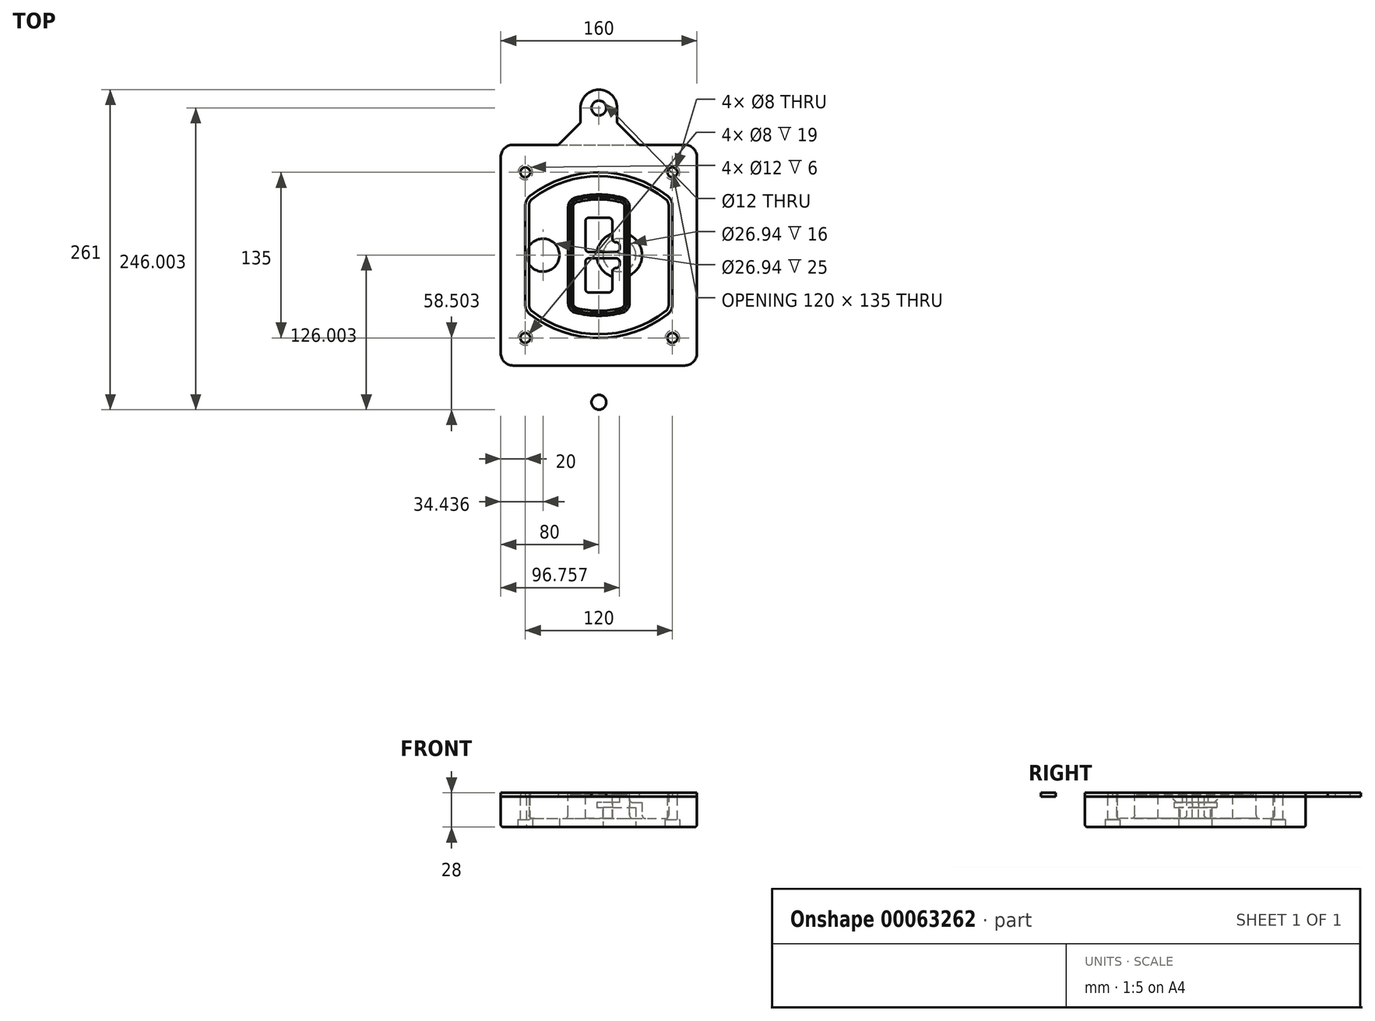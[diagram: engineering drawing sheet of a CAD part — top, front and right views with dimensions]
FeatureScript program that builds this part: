
annotation { "Feature Type Name" : "Feature", "Feature Type Description" : "" }
export const myFeature = defineFeature(function(context is Context, id is Id, definition is map)
    precondition{}
    {
        {
            var Q0;
            Q0=qCreatedBy(makeId("Top.planeOp"),FACE);
            var sketch = newSketch(context, id + "F0", { "sketchPlane" : qUnion([Q0])});
            skPoint(sketch, "E0.rect.middle", {"position": v(0, 0) * mm});
            skLineSegment(sketch, "E1.bottom", {"start": v(24.05, 28.38) * mm, "end": v(164.05, 28.38) * mm});
            skLineSegment(sketch, "E1.top", {"start": v(24.05, 208.38) * mm, "end": v(164.05, 208.38) * mm});
            skLineSegment(sketch, "E1.left", {"start": v(14.05, 38.38) * mm, "end": v(14.05, 198.38) * mm});
            skLineSegment(sketch, "E1.right", {"start": v(174.05, 38.38) * mm, "end": v(174.05, 198.38) * mm});
            skLineSegment(sketch, "E2", {"start": v(14.05, 208.38) * mm, "end": v(174.05, 28.38) * mm, "construction": true});
            skLineSegment(sketch, "E3", {"start": v(174.05, 208.38) * mm, "end": v(14.05, 28.38) * mm, "construction": true});
            skCircle(sketch, "E4", {"center": v(34.05, 185.88) * mm, "radius": 4 * mm});
            skCircle(sketch, "E5", {"center": v(154.05, 185.88) * mm, "radius": 4 * mm});
            skCircle(sketch, "E6", {"center": v(154.05, 50.88) * mm, "radius": 4 * mm});
            skCircle(sketch, "E7", {"center": v(34.05, 50.88) * mm, "radius": 4 * mm});
            skLineSegment(sketch, "E8", {"start": v(34.05, 185.88) * mm, "end": v(154.05, 185.88) * mm, "construction": true});
            skLineSegment(sketch, "E9", {"start": v(154.05, 185.88) * mm, "end": v(154.05, 50.88) * mm, "construction": true});
            skLineSegment(sketch, "E10", {"start": v(154.05, 50.88) * mm, "end": v(34.05, 50.88) * mm, "construction": true});
            skLineSegment(sketch, "E11", {"start": v(34.05, 50.88) * mm, "end": v(34.05, 185.88) * mm, "construction": true});
            skLineSegment(sketch, "E12", {"start": v(34.05, 158.68) * mm, "end": v(34.05, 78.09) * mm});
            skLineSegment(sketch, "E13", {"start": v(154.05, 158.68) * mm, "end": v(154.05, 78.09) * mm});
            skArc(sketch, "E14", {"start": v(150.2, 166.56) * mm, "mid": v(94.05, 185.88) * mm, "end": v(37.9, 166.56) * mm});
            skArc(sketch, "E15", {"start": v(37.9, 70.2) * mm, "mid": v(94.05, 50.88) * mm, "end": v(150.2, 70.2) * mm});
            skLineSegment(sketch, "E16", {"start": v(34.05, 118.38) * mm, "end": v(154.05, 118.38) * mm, "construction": true});
            skPoint(sketch, "E17.visualSharp", {"position": v(34.05, 73.38) * mm});
            skArc(sketch, "E17.filletArc", {"start": v(34.05, 78.09) * mm, "mid": v(35.06, 73.7) * mm, "end": v(37.9, 70.2) * mm});
            skPoint(sketch, "E18.visualSharp", {"position": v(34.05, 163.38) * mm});
            skArc(sketch, "E18.filletArc", {"start": v(37.9, 166.56) * mm, "mid": v(35.06, 163.06) * mm, "end": v(34.05, 158.68) * mm});
            skPoint(sketch, "E19.visualSharp", {"position": v(154.05, 163.38) * mm});
            skArc(sketch, "E19.filletArc", {"start": v(154.05, 158.68) * mm, "mid": v(153.04, 163.06) * mm, "end": v(150.2, 166.56) * mm});
            skPoint(sketch, "E20.visualSharp", {"position": v(154.05, 73.38) * mm});
            skArc(sketch, "E20.filletArc", {"start": v(150.2, 70.2) * mm, "mid": v(153.04, 73.7) * mm, "end": v(154.05, 78.09) * mm});
            skPoint(sketch, "E21.visualSharp", {"position": v(14.05, 208.38) * mm});
            skArc(sketch, "E21.filletArc", {"start": v(24.05, 208.38) * mm, "mid": v(16.98, 205.45) * mm, "end": v(14.05, 198.38) * mm});
            skPoint(sketch, "E22.visualSharp", {"position": v(174.05, 208.38) * mm});
            skArc(sketch, "E22.filletArc", {"start": v(174.05, 198.38) * mm, "mid": v(171.12, 205.45) * mm, "end": v(164.05, 208.38) * mm});
            skPoint(sketch, "E23.visualSharp", {"position": v(174.05, 28.38) * mm});
            skArc(sketch, "E23.filletArc", {"start": v(164.05, 28.38) * mm, "mid": v(171.12, 31.31) * mm, "end": v(174.05, 38.38) * mm});
            skPoint(sketch, "E24.visualSharp", {"position": v(14.05, 28.38) * mm});
            skArc(sketch, "E24.filletArc", {"start": v(14.05, 38.38) * mm, "mid": v(16.98, 31.31) * mm, "end": v(24.05, 28.38) * mm});
            skArc(sketch, "E25.0", {"start": v(151.05, 158.68) * mm, "mid": v(150.34, 161.75) * mm, "end": v(148.36, 164.2) * mm});
            skLineSegment(sketch, "E25.1", {"start": v(151.05, 158.68) * mm, "end": v(151.05, 78.09) * mm});
            skArc(sketch, "E25.2", {"start": v(148.36, 72.57) * mm, "mid": v(150.34, 75.02) * mm, "end": v(151.05, 78.09) * mm});
            skArc(sketch, "E25.3", {"start": v(39.74, 72.57) * mm, "mid": v(94.05, 53.88) * mm, "end": v(148.36, 72.57) * mm});
            skArc(sketch, "E25.4", {"start": v(37.05, 78.09) * mm, "mid": v(37.76, 75.02) * mm, "end": v(39.74, 72.57) * mm});
            skArc(sketch, "E25.5", {"start": v(148.36, 164.2) * mm, "mid": v(94.05, 182.88) * mm, "end": v(39.74, 164.2) * mm});
            skLineSegment(sketch, "E25.6", {"start": v(37.05, 158.68) * mm, "end": v(37.05, 78.09) * mm});
            skArc(sketch, "E25.7", {"start": v(39.74, 164.2) * mm, "mid": v(37.76, 161.75) * mm, "end": v(37.05, 158.68) * mm});
            skArc(sketch, "E26.0", {"start": v(35.43, 169.71) * mm, "mid": v(31.47, 164.82) * mm, "end": v(30.05, 158.68) * mm});
            skArc(sketch, "E26.1", {"start": v(152.67, 169.71) * mm, "mid": v(94.05, 189.88) * mm, "end": v(35.43, 169.71) * mm});
            skArc(sketch, "E26.2", {"start": v(158.05, 158.68) * mm, "mid": v(156.63, 164.82) * mm, "end": v(152.67, 169.71) * mm});
            skLineSegment(sketch, "E26.3", {"start": v(158.05, 158.68) * mm, "end": v(158.05, 78.09) * mm});
            skArc(sketch, "E26.4", {"start": v(152.67, 67.05) * mm, "mid": v(156.63, 71.95) * mm, "end": v(158.05, 78.09) * mm});
            skLineSegment(sketch, "E26.5", {"start": v(30.05, 158.68) * mm, "end": v(30.05, 78.09) * mm});
            skArc(sketch, "E26.6", {"start": v(35.43, 67.05) * mm, "mid": v(94.05, 46.88) * mm, "end": v(152.67, 67.05) * mm});
            skArc(sketch, "E26.7", {"start": v(30.05, 78.09) * mm, "mid": v(31.47, 71.95) * mm, "end": v(35.43, 67.05) * mm});
            skSolve(sketch);
        }
        {
            var Q0;
            Q0=makeQuery(id+"F0.imprint","IMPRINT",FACE,{"disambiguationData":[TD([[makeQuery(id+"F0.imprint","IMPRINT",EDGE,{"derivedFrom":sQuery(id+"F0.wireOp",EDGE,"E1.bottom")}),1.0]])]});
            var Q1;
            Q1=makeQuery(id+"F0.imprint","IMPRINT",FACE,{"disambiguationData":[TD([[makeQuery(id+"F0.imprint","IMPRINT",EDGE,{"derivedFrom":sQuery(id+"F0.wireOp",EDGE,"E12")}),1.0]])]});
            var Q2;
            Q2=makeQuery(id+"F0.imprint","IMPRINT",FACE,{"disambiguationData":[TD([[makeQuery(id+"F0.imprint","IMPRINT",EDGE,{"derivedFrom":sQuery(id+"F0.wireOp",EDGE,"E25.0")}),1.0]])]});
            var Q3;
            Q3=makeQuery(id+"F0.imprint","IMPRINT",FACE,{"disambiguationData":[TD([[makeQuery(id+"F0.imprint","IMPRINT",EDGE,{"derivedFrom":sQuery(id+"F0.wireOp",EDGE,"E12")}),-1.0]])]});
            extrude(context, id + "F1", {"entities" : qUnion([Q0, Q1, Q2, Q3]), "oppositeDirection" : true, "depth" : 25 * mm});
        }
        {
            var Q0;
            Q0=makeQuery(id+"F0.imprint","IMPRINT",FACE,{"disambiguationData":[TD([[makeQuery(id+"F0.imprint","IMPRINT",EDGE,{"derivedFrom":sQuery(id+"F0.wireOp",EDGE,"E12")}),1.0]])]});
            extrude(context, id + "F2", {"entities" : qUnion([Q0]), "operationType" : NewBodyOperationType.ADD, "depth" : 3 * mm});
        }
        {
            var Q0;
            Q0=makeQuery(id+"F0.imprint","IMPRINT",FACE,{"disambiguationData":[TD([[makeQuery(id+"F0.imprint","IMPRINT",EDGE,{"derivedFrom":sQuery(id+"F0.wireOp",EDGE,"E25.0")}),1.0]])]});
            extrude(context, id + "F3", {"entities" : qUnion([Q0]), "operationType" : NewBodyOperationType.REMOVE, "oppositeDirection" : true, "depth" : 18 * mm});
        }
        {
            var Q0;
            Q0=makeQuery(id+"F2.opExtrude","CAP_FACE",FACE,{"disambiguationData":[OSD([sQuery(id+"F0.wireOp",EDGE,"E12"),sQuery(id+"F0.wireOp",EDGE,"E13"),sQuery(id+"F0.wireOp",EDGE,"E14"),sQuery(id+"F0.wireOp",EDGE,"E15"),sQuery(id+"F0.wireOp",EDGE,"E17.filletArc"),sQuery(id+"F0.wireOp",EDGE,"E18.filletArc"),sQuery(id+"F0.wireOp",EDGE,"E19.filletArc"),sQuery(id+"F0.wireOp",EDGE,"E20.filletArc"),sQuery(id+"F0.wireOp",EDGE,"E25.0"),sQuery(id+"F0.wireOp",EDGE,"E25.1"),sQuery(id+"F0.wireOp",EDGE,"E25.2"),sQuery(id+"F0.wireOp",EDGE,"E25.3"),sQuery(id+"F0.wireOp",EDGE,"E25.4"),sQuery(id+"F0.wireOp",EDGE,"E25.5"),sQuery(id+"F0.wireOp",EDGE,"E25.6"),sQuery(id+"F0.wireOp",EDGE,"E25.7")])],"isStart":false});
            var sketch = newSketch(context, id + "F4", { "sketchPlane" : qUnion([Q0])});
            skArc(sketch, "E27.0", {"start": v(74.97, 71.41) * mm, "mid": v(94.05, 68.88) * mm, "end": v(113.13, 71.41) * mm});
            skArc(sketch, "E28.0", {"start": v(113.13, 165.35) * mm, "mid": v(94.05, 167.88) * mm, "end": v(74.97, 165.35) * mm});
            skLineSegment(sketch, "E29", {"start": v(69.05, 157.63) * mm, "end": v(69.05, 79.14) * mm});
            skLineSegment(sketch, "E30", {"start": v(119.05, 157.63) * mm, "end": v(119.05, 79.14) * mm});
            skLineSegment(sketch, "E31", {"start": v(69.05, 163.48) * mm, "end": v(119.05, 163.48) * mm, "construction": true});
            skLineSegment(sketch, "E32", {"start": v(69.05, 73.28) * mm, "end": v(119.05, 73.28) * mm, "construction": true});
            skPoint(sketch, "E33.visualSharp", {"position": v(69.05, 163.48) * mm});
            skArc(sketch, "E33.filletArc", {"start": v(74.97, 165.35) * mm, "mid": v(70.7, 162.5) * mm, "end": v(69.05, 157.63) * mm});
            skPoint(sketch, "E34.visualSharp", {"position": v(119.05, 163.48) * mm});
            skArc(sketch, "E34.filletArc", {"start": v(119.05, 157.63) * mm, "mid": v(117.4, 162.5) * mm, "end": v(113.13, 165.35) * mm});
            skPoint(sketch, "E35.visualSharp", {"position": v(119.05, 73.28) * mm});
            skArc(sketch, "E35.filletArc", {"start": v(113.13, 71.41) * mm, "mid": v(117.4, 74.27) * mm, "end": v(119.05, 79.14) * mm});
            skPoint(sketch, "E36.visualSharp", {"position": v(69.05, 73.28) * mm});
            skArc(sketch, "E36.filletArc", {"start": v(69.05, 79.14) * mm, "mid": v(70.7, 74.27) * mm, "end": v(74.97, 71.41) * mm});
            skArc(sketch, "E37.0", {"start": v(148.36, 164.2) * mm, "mid": v(94.05, 182.88) * mm, "end": v(39.74, 164.2) * mm});
            skArc(sketch, "E37.1", {"start": v(39.74, 164.2) * mm, "mid": v(37.76, 161.75) * mm, "end": v(37.05, 158.68) * mm});
            skLineSegment(sketch, "E37.2", {"start": v(37.05, 158.68) * mm, "end": v(37.05, 78.09) * mm});
            skArc(sketch, "E37.3", {"start": v(37.05, 78.09) * mm, "mid": v(37.76, 75.02) * mm, "end": v(39.74, 72.57) * mm});
            skArc(sketch, "E37.4", {"start": v(39.74, 72.57) * mm, "mid": v(94.05, 53.88) * mm, "end": v(148.36, 72.57) * mm});
            skArc(sketch, "E37.5", {"start": v(148.36, 72.57) * mm, "mid": v(150.34, 75.02) * mm, "end": v(151.05, 78.09) * mm});
            skLineSegment(sketch, "E37.6", {"start": v(151.05, 158.68) * mm, "end": v(151.05, 78.09) * mm});
            skArc(sketch, "E37.7", {"start": v(151.05, 158.68) * mm, "mid": v(150.34, 161.75) * mm, "end": v(148.36, 164.2) * mm});
            skLineSegment(sketch, "E38.0", {"start": v(117.05, 157.63) * mm, "end": v(117.05, 79.14) * mm});
            skArc(sketch, "E38.1", {"start": v(112.61, 73.34) * mm, "mid": v(115.81, 75.49) * mm, "end": v(117.05, 79.14) * mm});
            skArc(sketch, "E38.2", {"start": v(75.49, 73.34) * mm, "mid": v(94.05, 70.88) * mm, "end": v(112.61, 73.34) * mm});
            skArc(sketch, "E38.3", {"start": v(71.05, 79.14) * mm, "mid": v(72.29, 75.49) * mm, "end": v(75.49, 73.34) * mm});
            skLineSegment(sketch, "E38.4", {"start": v(71.05, 157.63) * mm, "end": v(71.05, 79.14) * mm});
            skArc(sketch, "E38.5", {"start": v(117.05, 157.63) * mm, "mid": v(115.81, 161.28) * mm, "end": v(112.61, 163.42) * mm});
            skArc(sketch, "E38.6", {"start": v(75.49, 163.42) * mm, "mid": v(72.29, 161.28) * mm, "end": v(71.05, 157.63) * mm});
            skArc(sketch, "E38.7", {"start": v(112.61, 163.42) * mm, "mid": v(94.05, 165.88) * mm, "end": v(75.49, 163.42) * mm});
            skArc(sketch, "E39.0", {"start": v(115.05, 157.63) * mm, "mid": v(114.23, 160.06) * mm, "end": v(112.1, 161.5) * mm});
            skLineSegment(sketch, "E39.1", {"start": v(115.05, 157.63) * mm, "end": v(115.05, 79.14) * mm});
            skArc(sketch, "E39.2", {"start": v(112.1, 75.27) * mm, "mid": v(114.23, 76.7) * mm, "end": v(115.05, 79.14) * mm});
            skArc(sketch, "E39.3", {"start": v(76, 75.27) * mm, "mid": v(94.05, 72.88) * mm, "end": v(112.1, 75.27) * mm});
            skArc(sketch, "E39.4", {"start": v(73.05, 79.14) * mm, "mid": v(73.87, 76.7) * mm, "end": v(76, 75.27) * mm});
            skArc(sketch, "E39.5", {"start": v(112.1, 161.5) * mm, "mid": v(94.05, 163.88) * mm, "end": v(76, 161.5) * mm});
            skLineSegment(sketch, "E39.6", {"start": v(73.05, 157.63) * mm, "end": v(73.05, 79.14) * mm});
            skArc(sketch, "E39.7", {"start": v(76, 161.5) * mm, "mid": v(73.87, 160.06) * mm, "end": v(73.05, 157.63) * mm});
            skLineSegment(sketch, "E40", {"start": v(69.05, 118.38) * mm, "end": v(119.05, 118.38) * mm, "construction": true});
            skLineSegment(sketch, "E41", {"start": v(83.05, 123.88) * mm, "end": v(83.05, 145.88) * mm});
            skLineSegment(sketch, "E42", {"start": v(86.05, 148.88) * mm, "end": v(102.05, 148.88) * mm});
            skLineSegment(sketch, "E43", {"start": v(105.05, 145.88) * mm, "end": v(105.05, 131.88) * mm});
            skLineSegment(sketch, "E44", {"start": v(108.05, 128.88) * mm, "end": v(108.05, 128.88) * mm});
            skLineSegment(sketch, "E45", {"start": v(111.05, 125.88) * mm, "end": v(111.05, 123.88) * mm});
            skLineSegment(sketch, "E46", {"start": v(108.05, 120.88) * mm, "end": v(86.05, 120.88) * mm});
            skPoint(sketch, "E47.visualSharp", {"position": v(83.05, 148.88) * mm});
            skArc(sketch, "E47.filletArc", {"start": v(86.05, 148.88) * mm, "mid": v(83.93, 148) * mm, "end": v(83.05, 145.88) * mm});
            skPoint(sketch, "E48.visualSharp", {"position": v(105.05, 148.88) * mm});
            skArc(sketch, "E48.filletArc", {"start": v(105.05, 145.88) * mm, "mid": v(104.17, 148) * mm, "end": v(102.05, 148.88) * mm});
            skPoint(sketch, "E49.visualSharp", {"position": v(105.05, 128.88) * mm});
            skArc(sketch, "E49.filletArc", {"start": v(105.05, 131.88) * mm, "mid": v(105.93, 129.76) * mm, "end": v(108.05, 128.88) * mm});
            skPoint(sketch, "E50.visualSharp", {"position": v(111.05, 128.88) * mm});
            skArc(sketch, "E50.filletArc", {"start": v(111.05, 125.88) * mm, "mid": v(110.17, 128) * mm, "end": v(108.05, 128.88) * mm});
            skPoint(sketch, "E51.visualSharp", {"position": v(111.05, 120.88) * mm});
            skArc(sketch, "E51.filletArc", {"start": v(108.05, 120.88) * mm, "mid": v(110.17, 121.76) * mm, "end": v(111.05, 123.88) * mm});
            skPoint(sketch, "E52.visualSharp", {"position": v(83.05, 120.88) * mm});
            skArc(sketch, "E52.filletArc", {"start": v(83.05, 123.88) * mm, "mid": v(83.93, 121.76) * mm, "end": v(86.05, 120.88) * mm});
            skLineSegment(sketch, "E53.0.MirrorCS", {"start": v(108.05, 115.88) * mm, "end": v(86.05, 115.88) * mm});
            skArc(sketch, "E54.0.MirrorCS", {"start": v(83.05, 112.88) * mm, "mid": v(83.93, 115) * mm, "end": v(86.05, 115.88) * mm});
            skLineSegment(sketch, "E55.0.MirrorCS", {"start": v(83.05, 112.88) * mm, "end": v(83.05, 90.88) * mm});
            skArc(sketch, "E56.0.MirrorCS", {"start": v(86.05, 87.88) * mm, "mid": v(83.93, 88.76) * mm, "end": v(83.05, 90.88) * mm});
            skLineSegment(sketch, "E57.0.MirrorCS", {"start": v(86.05, 87.88) * mm, "end": v(102.05, 87.88) * mm});
            skArc(sketch, "E58.0.MirrorCS", {"start": v(105.05, 90.88) * mm, "mid": v(104.17, 88.76) * mm, "end": v(102.05, 87.88) * mm});
            skLineSegment(sketch, "E59.0.MirrorCS", {"start": v(105.05, 90.88) * mm, "end": v(105.05, 104.88) * mm});
            skArc(sketch, "E60.0.MirrorCS", {"start": v(105.05, 104.88) * mm, "mid": v(105.93, 107) * mm, "end": v(108.05, 107.88) * mm});
            skArc(sketch, "E61.0.MirrorCS", {"start": v(111.05, 110.88) * mm, "mid": v(110.17, 108.76) * mm, "end": v(108.05, 107.88) * mm});
            skLineSegment(sketch, "E62.0.MirrorCS", {"start": v(111.05, 110.88) * mm, "end": v(111.05, 112.88) * mm});
            skArc(sketch, "E63.0.MirrorCS", {"start": v(108.05, 115.88) * mm, "mid": v(110.17, 115) * mm, "end": v(111.05, 112.88) * mm});
            skSolve(sketch);
        }
        {
            var Q0;
            Q0=makeQuery(id+"F4.imprint","IMPRINT",FACE,{"disambiguationData":[TD([[makeQuery(id+"F4.imprint","IMPRINT",EDGE,{"derivedFrom":sQuery(id+"F4.wireOp",EDGE,"E27.0")}),1.0]])]});
            var Q1;
            Q1=makeQuery(id+"F4.imprint","IMPRINT",FACE,{"disambiguationData":[TD([[makeQuery(id+"F4.imprint","IMPRINT",EDGE,{"derivedFrom":sQuery(id+"F4.wireOp",EDGE,"E38.0")}),-1.0]])]});
            var Q2;
            Q2=makeQuery(id+"F4.imprint","IMPRINT",FACE,{"disambiguationData":[TD([[makeQuery(id+"F4.imprint","IMPRINT",EDGE,{"derivedFrom":sQuery(id+"F4.wireOp",EDGE,"E39.0")}),1.0]])]});
            extrude(context, id + "F5", {"entities" : qUnion([Q0, Q1, Q2]), "operationType" : NewBodyOperationType.ADD, "endBound" : BoundingType.UP_TO_NEXT, "oppositeDirection" : true, "depth" : 25 * mm});
        }
        {
            var Q0;
            Q0=makeQuery(id+"F4.imprint","IMPRINT",FACE,{"disambiguationData":[TD([[makeQuery(id+"F4.imprint","IMPRINT",EDGE,{"derivedFrom":sQuery(id+"F4.wireOp",EDGE,"E38.0")}),-1.0]])]});
            extrude(context, id + "F6", {"entities" : qUnion([Q0]), "operationType" : NewBodyOperationType.REMOVE, "oppositeDirection" : true, "depth" : 2 * mm});
        }
        {
            var Q0;
            Q0=makeQuery(id+"F1.opExtrude","CAP_FACE",FACE,{"disambiguationData":[OSD([sQuery(id+"F0.wireOp",EDGE,"E1.bottom"),sQuery(id+"F0.wireOp",EDGE,"E1.top"),sQuery(id+"F0.wireOp",EDGE,"E1.left"),sQuery(id+"F0.wireOp",EDGE,"E1.right"),sQuery(id+"F0.wireOp",EDGE,"E4"),sQuery(id+"F0.wireOp",EDGE,"E5"),sQuery(id+"F0.wireOp",EDGE,"E6"),sQuery(id+"F0.wireOp",EDGE,"E7"),sQuery(id+"F0.wireOp",EDGE,"E21.filletArc"),sQuery(id+"F0.wireOp",EDGE,"E22.filletArc"),sQuery(id+"F0.wireOp",EDGE,"E23.filletArc"),sQuery(id+"F0.wireOp",EDGE,"E24.filletArc")])],"isStart":false});
            var sketch = newSketch(context, id + "F7", { "sketchPlane" : qUnion([Q0])});
            skCircle(sketch, "E64", {"center": v(110.8, -118.38) * mm, "radius": 13.47 * mm});
            skCircle(sketch, "E65", {"center": v(48.49, -118.38) * mm, "radius": 13.47 * mm});
            skLineSegment(sketch, "E66", {"start": v(174.05, -118.38) * mm, "end": v(14.05, -118.38) * mm});
            skCircle(sketch, "E67", {"center": v(110.8, -118.38) * mm, "radius": 18.47 * mm});
            skCircle(sketch, "E68", {"center": v(154.05, -185.88) * mm, "radius": 6 * mm});
            skCircle(sketch, "E69", {"center": v(34.05, -185.88) * mm, "radius": 6 * mm});
            skCircle(sketch, "E70", {"center": v(34.05, -50.88) * mm, "radius": 6 * mm});
            skCircle(sketch, "E71", {"center": v(154.05, -50.88) * mm, "radius": 6 * mm});
            skSolve(sketch);
        }
        {
            var Q0;
            {var subQ1=sQuery(id+"F7.wireOp",EDGE,"E66");var subQ4=sQuery(id+"F7.wireOp",EDGE,"E64");var subQ6=makeQuery(id+"F7.imprint","INTERSECT",VERTEX,{"disambiguationData":[OD(0.0)],"derivedFrom":[subQ4,subQ1]});Q0=makeQuery(id+"F7.imprint","IMPRINT",FACE,{"disambiguationData":[TD([[makeQuery(id+"F7.imprint","IMPRINT",EDGE,{"disambiguationData":[TD([[subQ6,-1.0]])],"derivedFrom":subQ4}),-1.0]])]});}
            var Q1;
            {var subQ0=sQuery(id+"F7.wireOp",EDGE,"E66");var subQ1=sQuery(id+"F7.wireOp",EDGE,"E64");var subQ3=makeQuery(id+"F7.imprint","INTERSECT",VERTEX,{"disambiguationData":[OD(0.0)],"derivedFrom":[subQ1,subQ0]});Q1=makeQuery(id+"F7.imprint","IMPRINT",FACE,{"disambiguationData":[TD([[makeQuery(id+"F7.imprint","IMPRINT",EDGE,{"disambiguationData":[TD([[subQ3,-1.0]])],"derivedFrom":subQ1}),1.0]])]});}
            var Q2;
            {var subQ0=sQuery(id+"F7.wireOp",EDGE,"E66");var subQ1=sQuery(id+"F7.wireOp",EDGE,"E64");var subQ3=makeQuery(id+"F7.imprint","INTERSECT",VERTEX,{"disambiguationData":[OD(0.0)],"derivedFrom":[subQ1,subQ0]});Q2=makeQuery(id+"F7.imprint","IMPRINT",FACE,{"disambiguationData":[TD([[makeQuery(id+"F7.imprint","IMPRINT",EDGE,{"disambiguationData":[TD([[subQ3,1.0]])],"derivedFrom":subQ1}),1.0]])]});}
            var Q3;
            {var subQ1=sQuery(id+"F7.wireOp",EDGE,"E66");var subQ4=sQuery(id+"F7.wireOp",EDGE,"E64");var subQ6=makeQuery(id+"F7.imprint","INTERSECT",VERTEX,{"disambiguationData":[OD(0.0)],"derivedFrom":[subQ4,subQ1]});Q3=makeQuery(id+"F7.imprint","IMPRINT",FACE,{"disambiguationData":[TD([[makeQuery(id+"F7.imprint","IMPRINT",EDGE,{"disambiguationData":[TD([[subQ6,1.0]])],"derivedFrom":subQ4}),-1.0]])]});}
            extrude(context, id + "F8", {"entities" : qUnion([Q0, Q1, Q2, Q3]), "operationType" : NewBodyOperationType.ADD, "oppositeDirection" : true, "depth" : 20 * mm});
        }
        {
            var Q0;
            {var subQ0=sQuery(id+"F7.wireOp",EDGE,"E66");var subQ1=sQuery(id+"F7.wireOp",EDGE,"E64");var subQ3=makeQuery(id+"F7.imprint","INTERSECT",VERTEX,{"disambiguationData":[OD(0.0)],"derivedFrom":[subQ1,subQ0]});Q0=makeQuery(id+"F7.imprint","IMPRINT",FACE,{"disambiguationData":[TD([[makeQuery(id+"F7.imprint","IMPRINT",EDGE,{"disambiguationData":[TD([[subQ3,-1.0]])],"derivedFrom":subQ1}),1.0]])]});}
            var Q1;
            {var subQ0=sQuery(id+"F7.wireOp",EDGE,"E66");var subQ1=sQuery(id+"F7.wireOp",EDGE,"E64");var subQ3=makeQuery(id+"F7.imprint","INTERSECT",VERTEX,{"disambiguationData":[OD(0.0)],"derivedFrom":[subQ1,subQ0]});Q1=makeQuery(id+"F7.imprint","IMPRINT",FACE,{"disambiguationData":[TD([[makeQuery(id+"F7.imprint","IMPRINT",EDGE,{"disambiguationData":[TD([[subQ3,1.0]])],"derivedFrom":subQ1}),1.0]])]});}
            extrude(context, id + "F9", {"entities" : qUnion([Q0, Q1]), "operationType" : NewBodyOperationType.REMOVE, "oppositeDirection" : true, "depth" : 16 * mm});
        }
        {
            var Q0;
            {var subQ0=sQuery(id+"F7.wireOp",EDGE,"E66");var subQ1=sQuery(id+"F7.wireOp",EDGE,"E65");var subQ3=makeQuery(id+"F7.imprint","INTERSECT",VERTEX,{"disambiguationData":[OD(0.0)],"derivedFrom":[subQ1,subQ0]});Q0=makeQuery(id+"F7.imprint","IMPRINT",FACE,{"disambiguationData":[TD([[makeQuery(id+"F7.imprint","IMPRINT",EDGE,{"disambiguationData":[TD([[subQ3,-1.0]])],"derivedFrom":subQ1}),1.0]])]});}
            var Q1;
            {var subQ0=sQuery(id+"F7.wireOp",EDGE,"E66");var subQ1=sQuery(id+"F7.wireOp",EDGE,"E65");var subQ3=makeQuery(id+"F7.imprint","INTERSECT",VERTEX,{"disambiguationData":[OD(0.0)],"derivedFrom":[subQ1,subQ0]});Q1=makeQuery(id+"F7.imprint","IMPRINT",FACE,{"disambiguationData":[TD([[makeQuery(id+"F7.imprint","IMPRINT",EDGE,{"disambiguationData":[TD([[subQ3,1.0]])],"derivedFrom":subQ1}),1.0]])]});}
            extrude(context, id + "F10", {"entities" : qUnion([Q0, Q1]), "operationType" : NewBodyOperationType.REMOVE, "oppositeDirection" : true, "depth" : 25 * mm});
        }
        {
            var Q0;
            Q0=makeQuery(id+"F7.imprint","IMPRINT",FACE,{"disambiguationData":[TD([[makeQuery(id+"F7.imprint","IMPRINT",EDGE,{"derivedFrom":sQuery(id+"F7.wireOp",EDGE,"E68")}),1.0]])]});
            var Q1;
            Q1=makeQuery(id+"F7.imprint","IMPRINT",FACE,{"disambiguationData":[TD([[makeQuery(id+"F7.imprint","IMPRINT",EDGE,{"derivedFrom":makeQuery(id+"F1.opExtrude","CAP_EDGE",EDGE,{"disambiguationData":[OSD([sQuery(id+"F0.wireOp",EDGE,"E5")])],"isStart":false})}),-1.0]])]});
            var Q2;
            Q2=makeQuery(id+"F7.imprint","IMPRINT",FACE,{"disambiguationData":[TD([[makeQuery(id+"F7.imprint","IMPRINT",EDGE,{"derivedFrom":sQuery(id+"F7.wireOp",EDGE,"E69")}),1.0]])]});
            var Q3;
            Q3=makeQuery(id+"F7.imprint","IMPRINT",FACE,{"disambiguationData":[TD([[makeQuery(id+"F7.imprint","IMPRINT",EDGE,{"derivedFrom":makeQuery(id+"F1.opExtrude","CAP_EDGE",EDGE,{"disambiguationData":[OSD([sQuery(id+"F0.wireOp",EDGE,"E4")])],"isStart":false})}),-1.0]])]});
            var Q4;
            Q4=makeQuery(id+"F7.imprint","IMPRINT",FACE,{"disambiguationData":[TD([[makeQuery(id+"F7.imprint","IMPRINT",EDGE,{"derivedFrom":sQuery(id+"F7.wireOp",EDGE,"E70")}),1.0]])]});
            var Q5;
            Q5=makeQuery(id+"F7.imprint","IMPRINT",FACE,{"disambiguationData":[TD([[makeQuery(id+"F7.imprint","IMPRINT",EDGE,{"derivedFrom":makeQuery(id+"F1.opExtrude","CAP_EDGE",EDGE,{"disambiguationData":[OSD([sQuery(id+"F0.wireOp",EDGE,"E7")])],"isStart":false})}),-1.0]])]});
            var Q6;
            Q6=makeQuery(id+"F7.imprint","IMPRINT",FACE,{"disambiguationData":[TD([[makeQuery(id+"F7.imprint","IMPRINT",EDGE,{"derivedFrom":sQuery(id+"F7.wireOp",EDGE,"E71")}),1.0]])]});
            var Q7;
            Q7=makeQuery(id+"F7.imprint","IMPRINT",FACE,{"disambiguationData":[TD([[makeQuery(id+"F7.imprint","IMPRINT",EDGE,{"derivedFrom":makeQuery(id+"F1.opExtrude","CAP_EDGE",EDGE,{"disambiguationData":[OSD([sQuery(id+"F0.wireOp",EDGE,"E6")])],"isStart":false})}),-1.0]])]});
            extrude(context, id + "F11", {"entities" : qUnion([Q0, Q1, Q2, Q3, Q4, Q5, Q6, Q7]), "operationType" : NewBodyOperationType.REMOVE, "oppositeDirection" : true, "depth" : 6 * mm});
        }
        {
            var Q0;
            Q0=makeQuery(id+"F9.boolean.opBoolean","COPY",FACE,{"derivedFrom":makeQuery(id+"F9.opExtrude","CAP_FACE",FACE,{"disambiguationData":[OSD([sQuery(id+"F7.wireOp",EDGE,"E64")])],"isStart":false})});
            var sketch = newSketch(context, id + "F12", { "sketchPlane" : qUnion([Q0])});
            skArc(sketch, "E72.0", {"start": v(105.05, -100.83) * mm, "mid": v(96.62, -106.56) * mm, "end": v(92.5, -115.88) * mm});
            skArc(sketch, "E72.1", {"start": v(92.5, -120.88) * mm, "mid": v(96.62, -130.2) * mm, "end": v(105.05, -135.93) * mm});
            skLineSegment(sketch, "E73", {"start": v(92.5, -120.88) * mm, "end": v(108.05, -120.88) * mm});
            skLineSegment(sketch, "E74.0", {"start": v(108.05, -115.88) * mm, "end": v(92.5, -115.88) * mm});
            skArc(sketch, "E74.1", {"start": v(108.05, -115.88) * mm, "mid": v(110.17, -115) * mm, "end": v(111.05, -112.88) * mm});
            skLineSegment(sketch, "E74.2", {"start": v(111.05, -110.88) * mm, "end": v(111.05, -112.88) * mm});
            skArc(sketch, "E74.3", {"start": v(111.05, -110.88) * mm, "mid": v(110.17, -108.76) * mm, "end": v(108.05, -107.88) * mm});
            skArc(sketch, "E74.4", {"start": v(105.05, -104.88) * mm, "mid": v(105.93, -107) * mm, "end": v(108.05, -107.88) * mm});
            skLineSegment(sketch, "E74.5", {"start": v(105.05, -100.83) * mm, "end": v(105.05, -104.88) * mm});
            skLineSegment(sketch, "E74.7", {"start": v(108.05, -120.88) * mm, "end": v(92.5, -120.88) * mm});
            skArc(sketch, "E74.8", {"start": v(108.05, -120.88) * mm, "mid": v(110.17, -121.76) * mm, "end": v(111.05, -123.88) * mm});
            skLineSegment(sketch, "E74.9", {"start": v(111.05, -125.88) * mm, "end": v(111.05, -123.88) * mm});
            skArc(sketch, "E74.10", {"start": v(111.05, -125.88) * mm, "mid": v(110.17, -128) * mm, "end": v(108.05, -128.88) * mm});
            skArc(sketch, "E74.11", {"start": v(105.05, -131.88) * mm, "mid": v(105.93, -129.76) * mm, "end": v(108.05, -128.88) * mm});
            skLineSegment(sketch, "E74.12", {"start": v(105.05, -135.93) * mm, "end": v(105.05, -131.88) * mm});
            skPoint(sketch, "E75.orphan", {"position": v(105.05, -145.88) * mm});
            skPoint(sketch, "E76.orphan", {"position": v(86.05, -120.88) * mm});
            skPoint(sketch, "E77.orphan", {"position": v(86.05, -115.88) * mm});
            skPoint(sketch, "E78.orphan", {"position": v(105.05, -90.88) * mm});
            skSolve(sketch);
        }
        {
            var Q0;
            {var subQ7=sQuery(id+"F12.wireOp",EDGE,"E72.0");var subQ14=sQuery(id+"F12.wireOp",EDGE,"E72.1");var subQ16=sQuery(id+"F12.wireOp",EDGE,"E74.1");var subQ18=sQuery(id+"F12.wireOp",EDGE,"E74.8");Q0=qUnion([makeQuery(id+"F12.imprint","IMPRINT",FACE,{"disambiguationData":[TD([[makeQuery(id+"F12.imprint","IMPRINT",EDGE,{"derivedFrom":subQ7}),1.0]])]}),makeQuery(id+"F12.imprint","IMPRINT",FACE,{"disambiguationData":[TD([[makeQuery(id+"F12.imprint","IMPRINT",EDGE,{"derivedFrom":subQ14}),1.0]])]}),makeQuery(id+"F12.imprint","IMPRINT",FACE,{"disambiguationData":[TD([[makeQuery(id+"F12.imprint","IMPRINT",EDGE,{"derivedFrom":subQ16}),1.0]])]}),makeQuery(id+"F12.imprint","IMPRINT",FACE,{"disambiguationData":[TD([[makeQuery(id+"F12.imprint","IMPRINT",EDGE,{"derivedFrom":subQ18}),-1.0]])]})]);}
            var Q1;
            Q1=makeQuery(id+"F5.boolean.opBoolean","SPLIT",FACE,{"disambiguationData":[TD([makeQuery(id+"F5.opExtrude","SWEPT_FACE",FACE,{"disambiguationData":[OSD([sQuery(id+"F4.wireOp",EDGE,"E41")])]})])],"derivedFrom":makeQuery(id+"F3.boolean.opBoolean","COPY",FACE,{"derivedFrom":makeQuery(id+"F3.opExtrude","CAP_FACE",FACE,{"disambiguationData":[OSD([sQuery(id+"F0.wireOp",EDGE,"E25.0"),sQuery(id+"F0.wireOp",EDGE,"E25.1"),sQuery(id+"F0.wireOp",EDGE,"E25.2"),sQuery(id+"F0.wireOp",EDGE,"E25.3"),sQuery(id+"F0.wireOp",EDGE,"E25.4"),sQuery(id+"F0.wireOp",EDGE,"E25.5"),sQuery(id+"F0.wireOp",EDGE,"E25.6"),sQuery(id+"F0.wireOp",EDGE,"E25.7")])],"isStart":false})})});
            extrude(context, id + "F13", {"entities" : qUnion([Q0]), "operationType" : NewBodyOperationType.REMOVE, "endBound" : BoundingType.UP_TO_SURFACE, "endBoundEntityFace" : qUnion([Q1]), "depth" : 25 * mm});
        }
        {
            var Q0;
            Q0=makeQuery(id+"F3.boolean.opBoolean","COPY",EDGE,{"derivedFrom":makeQuery(id+"F3.opExtrude","CAP_EDGE",EDGE,{"disambiguationData":[OSD([sQuery(id+"F0.wireOp",EDGE,"E25.6")])],"isStart":false})});
            var Q1;
            Q1=makeQuery(id+"F8.boolean.opBoolean","INTERSECT",EDGE,{"derivedFrom":[makeQuery(id+"F5.opExtrude","SWEPT_FACE",FACE,{"disambiguationData":[OSD([sQuery(id+"F4.wireOp",EDGE,"E30")])]}),makeQuery(id+"F8.opExtrude","CAP_FACE",FACE,{"disambiguationData":[OSD([sQuery(id+"F7.wireOp",EDGE,"E67")])],"isStart":false})]});
            var Q2;
            Q2=makeQuery(id+"F8.boolean.opBoolean","INTERSECT",EDGE,{"disambiguationData":[OD(1.0)],"derivedFrom":[makeQuery(id+"F5.opExtrude","SWEPT_FACE",FACE,{"disambiguationData":[OSD([sQuery(id+"F4.wireOp",EDGE,"E30")])]}),makeQuery(id+"F8.opExtrude","SWEPT_FACE",FACE,{"disambiguationData":[OSD([sQuery(id+"F7.wireOp",EDGE,"E67")])]})]});
            var Q3;
            {var subQ0=sQuery(id+"F4.wireOp",EDGE,"E30");Q3=makeQuery(id+"F8.boolean.opBoolean","SPLIT",EDGE,{"disambiguationData":[TD([makeQuery(id+"F5.opExtrude","SWEPT_FACE",FACE,{"disambiguationData":[OSD([sQuery(id+"F4.wireOp",EDGE,"E35.filletArc")])]})])],"derivedFrom":makeQuery(id+"F5.opExtrude","CAP_EDGE",EDGE,{"disambiguationData":[OSD([subQ0])],"isStart":false})});}
            var Q4;
            {var subQ0=sQuery(id+"F0.wireOp",EDGE,"E25.7");var subQ1=sQuery(id+"F0.wireOp",EDGE,"E25.1");var subQ2=sQuery(id+"F0.wireOp",EDGE,"E25.6");var subQ3=sQuery(id+"F0.wireOp",EDGE,"E25.5");var subQ4=sQuery(id+"F0.wireOp",EDGE,"E25.4");var subQ5=sQuery(id+"F0.wireOp",EDGE,"E25.0");var subQ6=sQuery(id+"F0.wireOp",EDGE,"E25.2");var subQ7=sQuery(id+"F0.wireOp",EDGE,"E25.3");Q4=makeQuery(id+"F8.boolean.opBoolean","INTERSECT",EDGE,{"derivedFrom":[makeQuery(id+"F5.boolean.opBoolean","SPLIT",FACE,{"disambiguationData":[TD([makeQuery(id+"F2.opExtrude","SWEPT_FACE",FACE,{"disambiguationData":[OSD([subQ5])]})])],"derivedFrom":makeQuery(id+"F3.boolean.opBoolean","COPY",FACE,{"derivedFrom":makeQuery(id+"F3.opExtrude","CAP_FACE",FACE,{"disambiguationData":[OSD([subQ5,subQ1,subQ6,subQ7,subQ4,subQ3,subQ2,subQ0])],"isStart":false})})}),makeQuery(id+"F8.opExtrude","SWEPT_FACE",FACE,{"disambiguationData":[OSD([sQuery(id+"F7.wireOp",EDGE,"E67")])]})]});}
            var Q5;
            Q5=makeQuery(id+"F8.boolean.opBoolean","INTERSECT",EDGE,{"disambiguationData":[OD(0.0)],"derivedFrom":[makeQuery(id+"F5.opExtrude","SWEPT_FACE",FACE,{"disambiguationData":[OSD([sQuery(id+"F4.wireOp",EDGE,"E30")])]}),makeQuery(id+"F8.opExtrude","SWEPT_FACE",FACE,{"disambiguationData":[OSD([sQuery(id+"F7.wireOp",EDGE,"E67")])]})]});
            fillet(context, id + "F14", {"entities" : qUnion([Q0, Q1, Q2, Q3, Q4, Q5]), "radius" : 3 * mm, "tangentPropagation" : true, "allowEdgeOverflow" : false});
        }
        {
            var Q0;
            Q0=makeQuery(id+"F1.opExtrude","CAP_EDGE",EDGE,{"disambiguationData":[OSD([sQuery(id+"F0.wireOp",EDGE,"E1.bottom")])],"isStart":false});
            fillet(context, id + "F15", {"entities" : qUnion([Q0]), "radius" : 2 * mm, "tangentPropagation" : true, "allowEdgeOverflow" : false});
        }
        {
            var Q0;
            {var subQ0=sQuery(id+"F0.wireOp",EDGE,"E22.filletArc");var subQ1=sQuery(id+"F0.wireOp",EDGE,"E7");var subQ2=sQuery(id+"F0.wireOp",EDGE,"E6");var subQ3=sQuery(id+"F0.wireOp",EDGE,"E5");var subQ4=sQuery(id+"F0.wireOp",EDGE,"E4");var subQ5=sQuery(id+"F0.wireOp",EDGE,"E1.bottom");var subQ6=sQuery(id+"F0.wireOp",EDGE,"E21.filletArc");var subQ7=sQuery(id+"F0.wireOp",EDGE,"E1.top");var subQ8=sQuery(id+"F0.wireOp",EDGE,"E1.left");var subQ9=sQuery(id+"F0.wireOp",EDGE,"E1.right");var subQ10=sQuery(id+"F0.wireOp",EDGE,"E23.filletArc");var subQ11=sQuery(id+"F0.wireOp",EDGE,"E24.filletArc");Q0=makeQuery(id+"F2.boolean.opBoolean","SPLIT",FACE,{"disambiguationData":[TD([makeQuery(id+"F1.opExtrude","SWEPT_FACE",FACE,{"disambiguationData":[OSD([subQ5])]})])],"derivedFrom":makeQuery(id+"F1.opExtrude","CAP_FACE",FACE,{"disambiguationData":[OSD([subQ5,subQ7,subQ8,subQ9,subQ4,subQ3,subQ2,subQ1,subQ6,subQ0,subQ10,subQ11])],"isStart":true})});}
            var sketch = newSketch(context, id + "F16", { "sketchPlane" : qUnion([Q0])});
            skCircle(sketch, "E79", {"center": v(94.05, 238.38) * mm, "radius": 6 * mm});
            skArc(sketch, "E80", {"start": v(109.05, 238.38) * mm, "mid": v(94.05, 253.38) * mm, "end": v(79.05, 238.38) * mm});
            skLineSegment(sketch, "E81", {"start": v(79.05, 238.38) * mm, "end": v(79.05, 226.38) * mm});
            skLineSegment(sketch, "E82", {"start": v(79.05, 226.38) * mm, "end": v(61.05, 208.38) * mm});
            skLineSegment(sketch, "E83", {"start": v(109.05, 238.38) * mm, "end": v(109.05, 226.38) * mm});
            skLineSegment(sketch, "E84", {"start": v(109.05, 226.38) * mm, "end": v(127.05, 208.38) * mm});
            skLineSegment(sketch, "E85", {"start": v(94.05, 238.38) * mm, "end": v(94.05, 208.38) * mm, "construction": true});
            skLineSegment(sketch, "E86", {"start": v(14.05, 118.38) * mm, "end": v(174.05, 118.38) * mm, "construction": true});
            skCircle(sketch, "E87.MirrorC", {"center": v(94.05, -1.62) * mm, "radius": 6 * mm});
            skLineSegment(sketch, "E88.MirrorCS", {"start": v(79.05, 10.38) * mm, "end": v(61.05, 28.38) * mm});
            skLineSegment(sketch, "E89.MirrorCS", {"start": v(79.05, -1.62) * mm, "end": v(79.05, 10.38) * mm});
            skLineSegment(sketch, "E90.MirrorCS", {"start": v(109.05, -1.62) * mm, "end": v(109.05, 10.38) * mm});
            skLineSegment(sketch, "E91.MirrorCS", {"start": v(109.05, 10.38) * mm, "end": v(127.05, 28.38) * mm});
            skArc(sketch, "E92.MirrorCS", {"start": v(109.05, -1.62) * mm, "mid": v(94.05, -16.62) * mm, "end": v(79.05, -1.62) * mm});
            skLineSegment(sketch, "E93.MirrorCS", {"start": v(94.05, -1.62) * mm, "end": v(94.05, 28.38) * mm, "construction": true});
            skSolve(sketch);
        }
        {
            var Q0;
            Q0=makeQuery(id+"F16.imprint","IMPRINT",FACE,{"disambiguationData":[TD([[makeQuery(id+"F16.imprint","IMPRINT",EDGE,{"derivedFrom":sQuery(id+"F16.wireOp",EDGE,"E79")}),-1.0]])]});
            var Q1;
            Q1=makeQuery(id+"F16.imprint","IMPRINT",FACE,{"disambiguationData":[TD([[makeQuery(id+"F16.imprint","IMPRINT",EDGE,{"derivedFrom":makeQuery(id+"F1.opExtrude","CAP_EDGE",EDGE,{"disambiguationData":[OSD([sQuery(id+"F0.wireOp",EDGE,"E1.left")])],"isStart":true})}),-1.0]])]});
            var Q2;
            Q2=makeQuery(id+"F16.imprint","IMPRINT",FACE,{"disambiguationData":[TD([[makeQuery(id+"F16.imprint","IMPRINT",EDGE,{"derivedFrom":sQuery(id+"F16.wireOp",EDGE,"E87.MirrorC")}),1.0]])]});
            var Q3;
            Q3=makeQuery(id+"F2.opExtrude","CAP_FACE",FACE,{"disambiguationData":[OSD([sQuery(id+"F0.wireOp",EDGE,"E12"),sQuery(id+"F0.wireOp",EDGE,"E13"),sQuery(id+"F0.wireOp",EDGE,"E14"),sQuery(id+"F0.wireOp",EDGE,"E15"),sQuery(id+"F0.wireOp",EDGE,"E17.filletArc"),sQuery(id+"F0.wireOp",EDGE,"E18.filletArc"),sQuery(id+"F0.wireOp",EDGE,"E19.filletArc"),sQuery(id+"F0.wireOp",EDGE,"E20.filletArc"),sQuery(id+"F0.wireOp",EDGE,"E25.0"),sQuery(id+"F0.wireOp",EDGE,"E25.1"),sQuery(id+"F0.wireOp",EDGE,"E25.2"),sQuery(id+"F0.wireOp",EDGE,"E25.3"),sQuery(id+"F0.wireOp",EDGE,"E25.4"),sQuery(id+"F0.wireOp",EDGE,"E25.5"),sQuery(id+"F0.wireOp",EDGE,"E25.6"),sQuery(id+"F0.wireOp",EDGE,"E25.7")])],"isStart":false});
            extrude(context, id + "F17", {"entities" : qUnion([Q0, Q1, Q2]), "endBound" : BoundingType.UP_TO_SURFACE, "endBoundEntityFace" : qUnion([Q3]), "depth" : 25 * mm});
        }
    });
